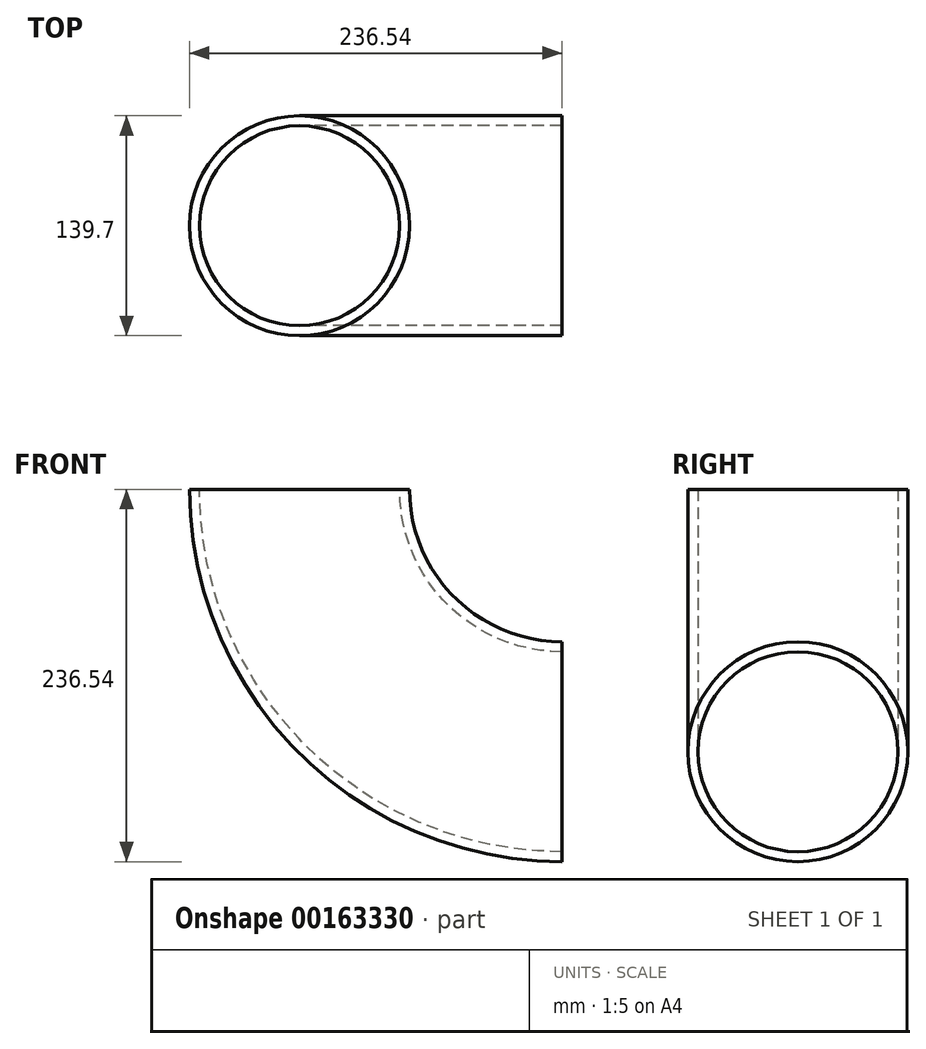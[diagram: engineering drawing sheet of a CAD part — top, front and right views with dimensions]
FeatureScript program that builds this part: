
annotation { "Feature Type Name" : "Feature", "Feature Type Description" : "" }
export const myFeature = defineFeature(function(context is Context, id is Id, definition is map)
    precondition{}
    {
        {
            var Q0;
            Q0=qCreatedBy(makeId("Top.planeOp"),FACE);
            var sketch = newSketch(context, id + "F0", { "sketchPlane" : qUnion([Q0])});
            skCircle(sketch, "E0", {"center": v(0, 0) * mm, "radius": 63.5 * mm});
            skCircle(sketch, "E1", {"center": v(0, 0) * mm, "radius": 69.85 * mm});
            skLineSegment(sketch, "E2", {"start": v(166.69, 74.23) * mm, "end": v(166.69, -76.34) * mm});
            skSolve(sketch);
        }
        {
            var Q0;
            Q0=makeQuery(id+"F0.imprint","IMPRINT",FACE,{"disambiguationData":[TD([[makeQuery(id+"F0.imprint","IMPRINT",EDGE,{"derivedFrom":sQuery(id+"F0.wireOp",EDGE,"E0")}),-1.0]])]});
            var Q1;
            Q1=sQuery(id+"F0.wireOp",EDGE,"E2");
            revolve(context, id + "F1", {"entities" : qUnion([Q0]), "axis" : qUnion([Q1]), "revolveType" : RevolveType.ONE_DIRECTION, "angle" : 90 * degree});
        }
    });
